# Revit family: 701010001 EBF-750
name_source: partatom
category: Aparatos sanitarios
revit_build: Autodesk Revit 2018 (Build: 20170223_1515(x64)
units: mm (PartAtom-declared; Revit-internal decimal feet)

## family parameters
Compartido = Sí
Corte con vacíos al cargar = No
Cota de conector redondo = Diámetro de uso
Número OmniClass = 23.45.55.17
Punto de cálculo de habitación = No
Se basa en plano de trabajo = Sí
Siempre vertical = Sí
Tipo de pieza = Normal
Título OmniClass = Mixing Faucets

## types (1)
- EBF-750
    ADA Compliant = Sí
    Accionamiento = Sensor
    Conexión AC = Sí
    Conexión AF = Sí
    Conexión de residuos = No
    Conexión de ventilación = No
    Consumo de agua = 8,3 l/m
    Código de montaje = D2010300
    Descripción = Battery Powered Sensor Activated Electronic Gooseneck Hand Washing Faucet for tempered or hot/cold water operation.
    Diámetro de conexión = 1/2 pulg. NPSM / de la manguera
    Elevación por defecto = 0 mm
    Fabricante = SLOAN
    Finish(es) = CP, PVDSF, PVDPB, PVDBN
    Fixture Color = Not Applicable
    Flush Volume(s)/Flow Rate(s) = 2.2 gpm/8.3 Lpm Laminar Flow Spray Head
    Garantía = 3 años por Defectos de fabricación y cromados
1 año por sistema electrico
    IAPMO Certification = Low Lead cUPC
    Material = Chrome Plated
    Material de fabricación = Latón
    Modelo = EBF-750
    Mounting = Deck-Mount
    Nombre = Grifería Lavamanos Cuello de Ganzo
    Operation = Sensor-Activated
    Presión Máxima = 80 Psi.
    Presión mínima = 20 Psi.
    Referencia = 701010001
    Revised Date = 26/08/2013
    Tipo = Grifería Lavamanos
    Tráfico = Institucional Alto Tráfico
    URL = https://www.corona.co
    Vida útil = 150000 ciclos
    Warranty = 3 Year (Limited)

## geometry (parser evidence)
native form markers: Sweep x2
no freeform markers — native parametric forms only
